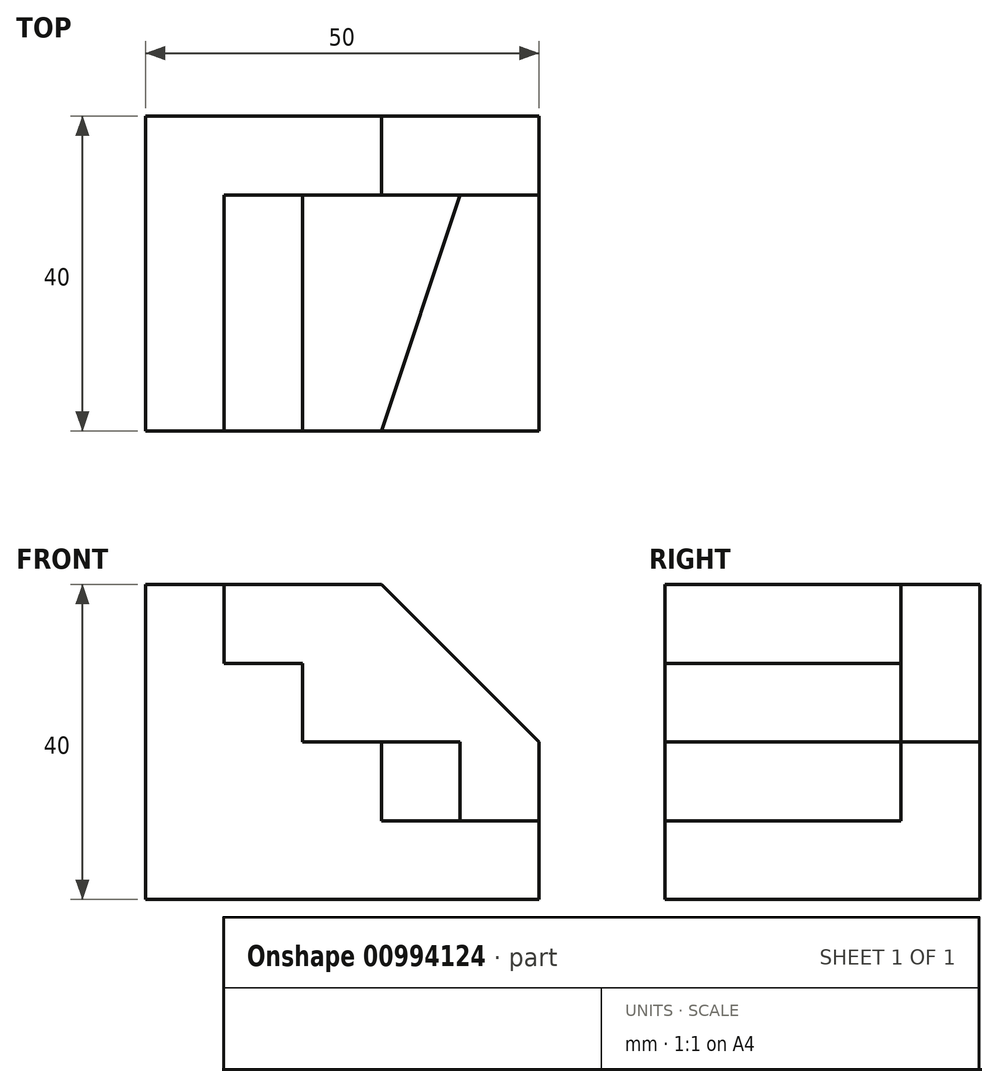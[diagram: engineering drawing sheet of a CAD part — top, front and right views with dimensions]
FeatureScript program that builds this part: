
annotation { "Feature Type Name" : "Feature", "Feature Type Description" : "" }
export const myFeature = defineFeature(function(context is Context, id is Id, definition is map)
    precondition{}
    {
        {
            var Q0;
            Q0=qCreatedBy(makeId("Top.planeOp"),FACE);
            var sketch = newSketch(context, id + "F0", { "sketchPlane" : qUnion([Q0])});
            skLineSegment(sketch, "E0.bottom", {"start": v(0, 0) * mm, "end": v(50, 0) * mm});
            skLineSegment(sketch, "E0.top", {"start": v(0, 40) * mm, "end": v(50, 40) * mm});
            skLineSegment(sketch, "E0.left", {"start": v(0, 0) * mm, "end": v(0, 40) * mm});
            skLineSegment(sketch, "E0.right", {"start": v(50, 0) * mm, "end": v(50, 40) * mm});
            skSolve(sketch);
        }
        {
            var Q0;
            Q0=makeQuery(id+"F0.imprint","IMPRINT",FACE,{"disambiguationData":[TD([[makeQuery(id+"F0.imprint","IMPRINT",EDGE,{"derivedFrom":sQuery(id+"F0.wireOp",EDGE,"E0.bottom")}),1.0]])]});
            extrude(context, id + "F1", {"entities" : qUnion([Q0]), "depth" : 40 * mm, "offsetDistance" : 25 * mm});
        }
        {
            var Q0;
            Q0=makeQuery(id+"F1.opExtrude","CAP_FACE",FACE,{"disambiguationData":[OSD([sQuery(id+"F0.wireOp",EDGE,"E0.bottom"),sQuery(id+"F0.wireOp",EDGE,"E0.top"),sQuery(id+"F0.wireOp",EDGE,"E0.left"),sQuery(id+"F0.wireOp",EDGE,"E0.right")])],"isStart":false});
            var sketch = newSketch(context, id + "F2", { "sketchPlane" : qUnion([Q0])});
            skLineSegment(sketch, "E1.0", {"start": v(0, 40) * mm, "end": v(50, 40) * mm});
            skLineSegment(sketch, "E2.0", {"start": v(0, 0) * mm, "end": v(0, 40) * mm});
            skLineSegment(sketch, "E3.0", {"start": v(50, 0) * mm, "end": v(50, 40) * mm});
            skLineSegment(sketch, "E4.0", {"start": v(0, 0) * mm, "end": v(50, 0) * mm});
            skLineSegment(sketch, "E5.0", {"start": v(10, 30) * mm, "end": v(50, 30) * mm});
            skLineSegment(sketch, "E5.1", {"start": v(10, 0) * mm, "end": v(10, 30) * mm});
            skSolve(sketch);
        }
        {
            var Q0;
            {var subQ3=sQuery(id+"F2.wireOp",EDGE,"E5.0");Q0=makeQuery(id+"F2.imprint","IMPRINT",FACE,{"disambiguationData":[TD([[makeQuery(id+"F2.imprint","IMPRINT",EDGE,{"derivedFrom":subQ3}),-1.0]])]});}
            extrude(context, id + "F3", {"entities" : qUnion([Q0]), "operationType" : NewBodyOperationType.REMOVE, "oppositeDirection" : true, "depth" : 30 * mm, "offsetDistance" : 25 * mm});
        }
        {
            var Q0;
            Q0=makeQuery(id+"F3.boolean.opBoolean","COPY",FACE,{"derivedFrom":makeQuery(id+"F3.opExtrude","SWEPT_FACE",FACE,{"disambiguationData":[OSD([sQuery(id+"F2.wireOp",EDGE,"E5.0")])]})});
            var sketch = newSketch(context, id + "F4", { "sketchPlane" : qUnion([Q0])});
            skLineSegment(sketch, "E6", {"start": v(30, 40) * mm, "end": v(50, 20) * mm});
            skSolve(sketch);
        }
        {
            var Q0;
            {var subQ0=sQuery(id+"F4.wireOp",EDGE,"E6");Q0=makeQuery(id+"F4.imprint","IMPRINT",FACE,{"disambiguationData":[TD([[makeQuery(id+"F4.imprint","IMPRINT",EDGE,{"derivedFrom":subQ0}),1.0]])]});}
            extrude(context, id + "F5", {"entities" : qUnion([Q0]), "operationType" : NewBodyOperationType.REMOVE, "endBound" : BoundingType.THROUGH_ALL, "oppositeDirection" : true, "depth" : 25 * mm, "offsetDistance" : 25 * mm});
        }
        {
            var Q0;
            Q0=makeQuery(id+"F3.boolean.opBoolean","COPY",FACE,{"derivedFrom":makeQuery(id+"F3.opExtrude","CAP_FACE",FACE,{"disambiguationData":[OSD([sQuery(id+"F2.wireOp",EDGE,"E3.0"),sQuery(id+"F2.wireOp",EDGE,"E4.0"),sQuery(id+"F2.wireOp",EDGE,"E5.0"),sQuery(id+"F2.wireOp",EDGE,"E5.1")])],"isStart":false})});
            var sketch = newSketch(context, id + "F6", { "sketchPlane" : qUnion([Q0])});
            skLineSegment(sketch, "E7.0.0", {"start": v(10, 30) * mm, "end": v(10, 0) * mm});
            skLineSegment(sketch, "E7.0.1", {"start": v(10, 0) * mm, "end": v(50, 0) * mm});
            skLineSegment(sketch, "E7.0.2", {"start": v(50, 0) * mm, "end": v(50, 30) * mm});
            skLineSegment(sketch, "E7.0.3", {"start": v(50, 30) * mm, "end": v(10, 30) * mm});
            skLineSegment(sketch, "E8", {"start": v(20, 0) * mm, "end": v(20, 30) * mm});
            skLineSegment(sketch, "E9", {"start": v(30, 0) * mm, "end": v(40, 30) * mm});
            skSolve(sketch);
        }
        {
            var Q0;
            {var subQ0=sQuery(id+"F6.wireOp",EDGE,"E7.0.0");Q0=makeQuery(id+"F6.imprint","IMPRINT",FACE,{"disambiguationData":[TD([[makeQuery(id+"F6.imprint","IMPRINT",EDGE,{"derivedFrom":subQ0}),-1.0]])]});}
            extrude(context, id + "F7", {"entities" : qUnion([Q0]), "operationType" : NewBodyOperationType.ADD, "depth" : 20 * mm, "offsetDistance" : 25 * mm});
        }
        {
            var Q0;
            {var subQ0=sQuery(id+"F6.wireOp",EDGE,"E8");Q0=makeQuery(id+"F6.imprint","IMPRINT",FACE,{"disambiguationData":[TD([[makeQuery(id+"F6.imprint","IMPRINT",EDGE,{"derivedFrom":subQ0}),-1.0]])]});}
            extrude(context, id + "F8", {"entities" : qUnion([Q0]), "operationType" : NewBodyOperationType.ADD, "depth" : 10 * mm, "offsetDistance" : 25 * mm});
        }
    });
